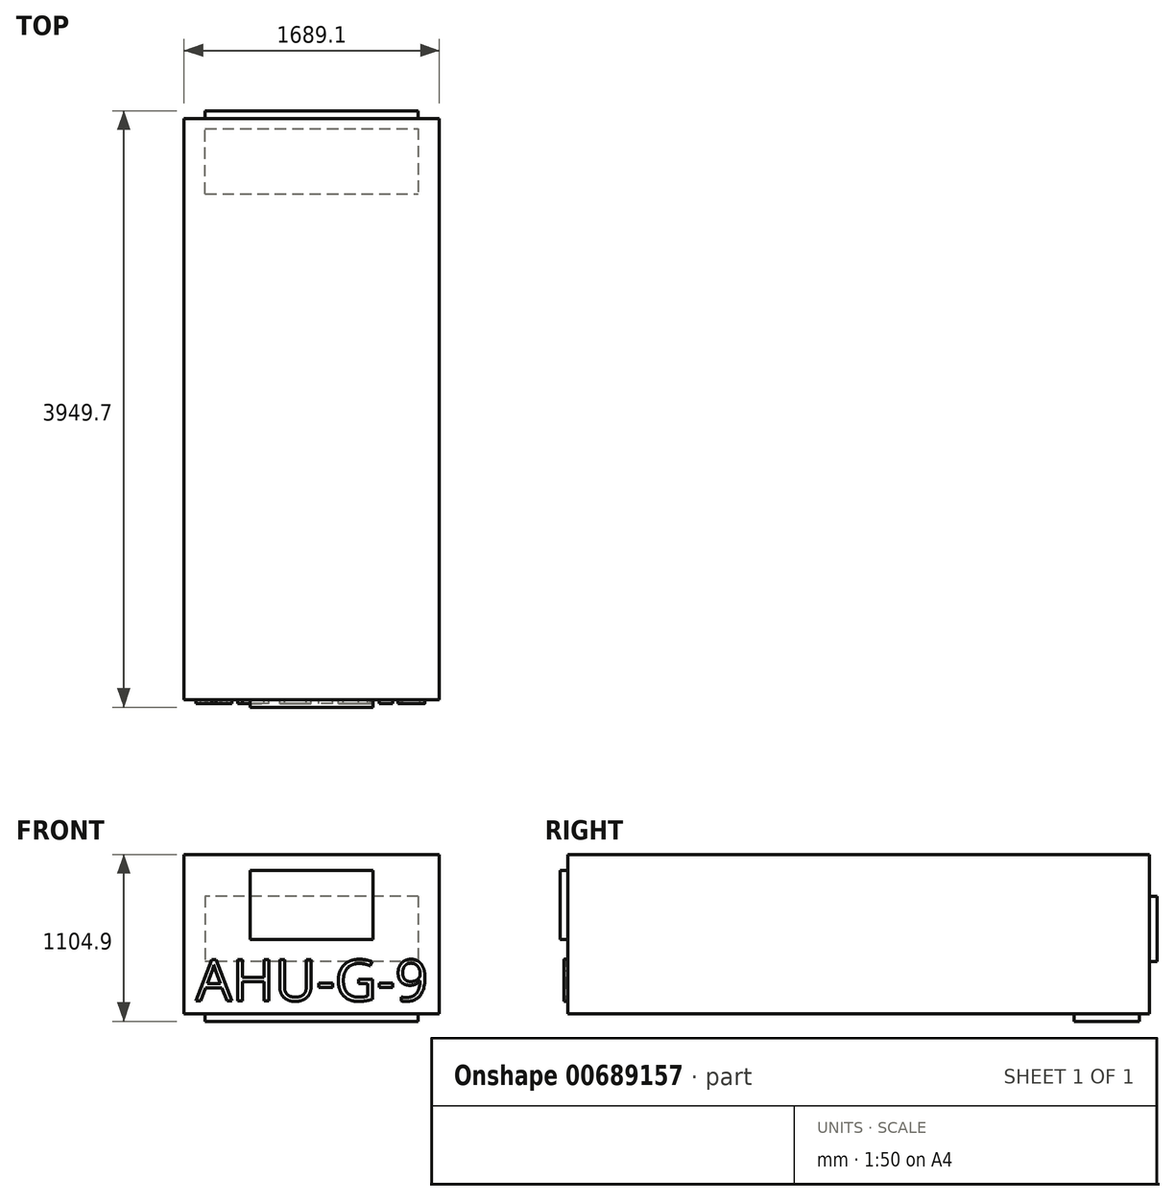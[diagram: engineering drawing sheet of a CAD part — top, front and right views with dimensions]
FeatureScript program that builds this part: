
annotation { "Feature Type Name" : "Feature", "Feature Type Description" : "" }
export const myFeature = defineFeature(function(context is Context, id is Id, definition is map)
    precondition{}
    {
        {
            var Q0;
            Q0=qCreatedBy(makeId("Front.planeOp"),FACE);
            var sketch = newSketch(context, id + "F0", { "sketchPlane" : qUnion([Q0])});
            skLineSegment(sketch, "E0.bottom", {"start": v(-639.94, 501.66) * mm, "end": v(1049.16, 501.66) * mm});
            skLineSegment(sketch, "E0.top", {"start": v(-639.94, -552.44) * mm, "end": v(1049.16, -552.44) * mm});
            skLineSegment(sketch, "E0.left", {"start": v(-639.94, 501.66) * mm, "end": v(-639.94, -552.44) * mm});
            skLineSegment(sketch, "E0.right", {"start": v(1049.16, 501.66) * mm, "end": v(1049.16, -552.44) * mm});
            skSolve(sketch);
        }
        {
            var Q0;
            Q0=qSketchRegion(id+"F0",true);
            extrude(context, id + "F1", {"entities" : qUnion([Q0]), "depth" : 3848.1 * mm, "offsetDistance" : 25.4 * mm});
        }
        {
            var Q0;
            Q0=makeQuery(id+"F1.opExtrude","CAP_FACE",FACE,{"disambiguationData":[OSD([sQuery(id+"F0.wireOp",EDGE,"E0.bottom"),sQuery(id+"F0.wireOp",EDGE,"E0.top"),sQuery(id+"F0.wireOp",EDGE,"E0.left"),sQuery(id+"F0.wireOp",EDGE,"E0.right")])],"isStart":false});
            var sketch = newSketch(context, id + "F2", { "sketchPlane" : qUnion([Q0])});
            skLineSegment(sketch, "E1.bottom", {"start": v(-201.8, 396.89) * mm, "end": v(611, 396.89) * mm});
            skLineSegment(sketch, "E1.top", {"start": v(-201.8, -60.31) * mm, "end": v(611, -60.31) * mm});
            skLineSegment(sketch, "E1.left", {"start": v(-201.8, 396.89) * mm, "end": v(-201.8, -60.31) * mm});
            skLineSegment(sketch, "E1.right", {"start": v(611, 396.89) * mm, "end": v(611, -60.31) * mm});
            skSolve(sketch);
        }
        {
            var Q0;
            Q0=makeQuery(id+"F2.imprint","IMPRINT",FACE,{"disambiguationData":[TD([[makeQuery(id+"F2.imprint","IMPRINT",EDGE,{"derivedFrom":sQuery(id+"F2.wireOp",EDGE,"E1.bottom")}),-1.0]])]});
            extrude(context, id + "F3", {"entities" : qUnion([Q0]), "operationType" : NewBodyOperationType.ADD, "depth" : 50.8 * mm, "offsetDistance" : 25.4 * mm});
        }
        {
            var Q0;
            Q0=makeQuery(id+"F1.opExtrude","CAP_FACE",FACE,{"disambiguationData":[OSD([sQuery(id+"F0.wireOp",EDGE,"E0.bottom"),sQuery(id+"F0.wireOp",EDGE,"E0.top"),sQuery(id+"F0.wireOp",EDGE,"E0.left"),sQuery(id+"F0.wireOp",EDGE,"E0.right")])],"isStart":false});
            var sketch = newSketch(context, id + "F4", { "sketchPlane" : qUnion([Q0])});
            skText(sketch, "E2", { "text": "AHU-G-9", "fontName": "OpenSans-Regular.ttf"});
            const initialGuessF4  = {"E2": [-0.56358, -0.46768, 1, 0, 0.27381]};
            skSetInitialGuess(sketch, initialGuessF4);
            skSolve(sketch);
        }
        {
            var Q0;
            Q0=qSketchRegion(id+"F4",true);
            extrude(context, id + "F5", {"entities" : qUnion([Q0]), "operationType" : NewBodyOperationType.ADD, "depth" : 25.4 * mm, "offsetDistance" : 25.4 * mm});
        }
        {
            var Q0;
            Q0=makeQuery(id+"F1.opExtrude","CAP_FACE",FACE,{"disambiguationData":[OSD([sQuery(id+"F0.wireOp",EDGE,"E0.bottom"),sQuery(id+"F0.wireOp",EDGE,"E0.top"),sQuery(id+"F0.wireOp",EDGE,"E0.left"),sQuery(id+"F0.wireOp",EDGE,"E0.right")])],"isStart":true});
            var sketch = newSketch(context, id + "F6", { "sketchPlane" : qUnion([Q0])});
            skLineSegment(sketch, "E3.bottom", {"start": v(-909.46, 225.44) * mm, "end": v(500.24, 225.44) * mm});
            skLineSegment(sketch, "E3.top", {"start": v(-909.46, -206.36) * mm, "end": v(500.24, -206.36) * mm});
            skLineSegment(sketch, "E3.left", {"start": v(-909.46, 225.44) * mm, "end": v(-909.46, -206.36) * mm});
            skLineSegment(sketch, "E3.right", {"start": v(500.24, 225.44) * mm, "end": v(500.24, -206.36) * mm});
            skSolve(sketch);
        }
        {
            var Q0;
            Q0=qSketchRegion(id+"F6",true);
            extrude(context, id + "F7", {"entities" : qUnion([Q0]), "operationType" : NewBodyOperationType.ADD, "depth" : 50.8 * mm, "offsetDistance" : 25.4 * mm});
        }
        {
            var Q0;
            Q0=makeQuery(id+"F1.opExtrude","SWEPT_FACE",FACE,{"disambiguationData":[OSD([sQuery(id+"F0.wireOp",EDGE,"E0.top")])]});
            var sketch = newSketch(context, id + "F8", { "sketchPlane" : qUnion([Q0])});
            skLineSegment(sketch, "E4.bottom", {"start": v(-500.24, 66.67) * mm, "end": v(909.46, 66.68) * mm});
            skLineSegment(sketch, "E4.top", {"start": v(-500.24, 498.47) * mm, "end": v(909.46, 498.48) * mm});
            skLineSegment(sketch, "E4.left", {"start": v(-500.24, 498.47) * mm, "end": v(-500.24, 66.67) * mm});
            skLineSegment(sketch, "E4.right", {"start": v(909.46, 66.68) * mm, "end": v(909.46, 498.48) * mm});
            skSolve(sketch);
        }
        {
            var Q0;
            Q0=qSketchRegion(id+"F8",true);
            extrude(context, id + "F9", {"entities" : qUnion([Q0]), "operationType" : NewBodyOperationType.ADD, "depth" : 50.8 * mm, "offsetDistance" : 25.4 * mm});
        }
    });
